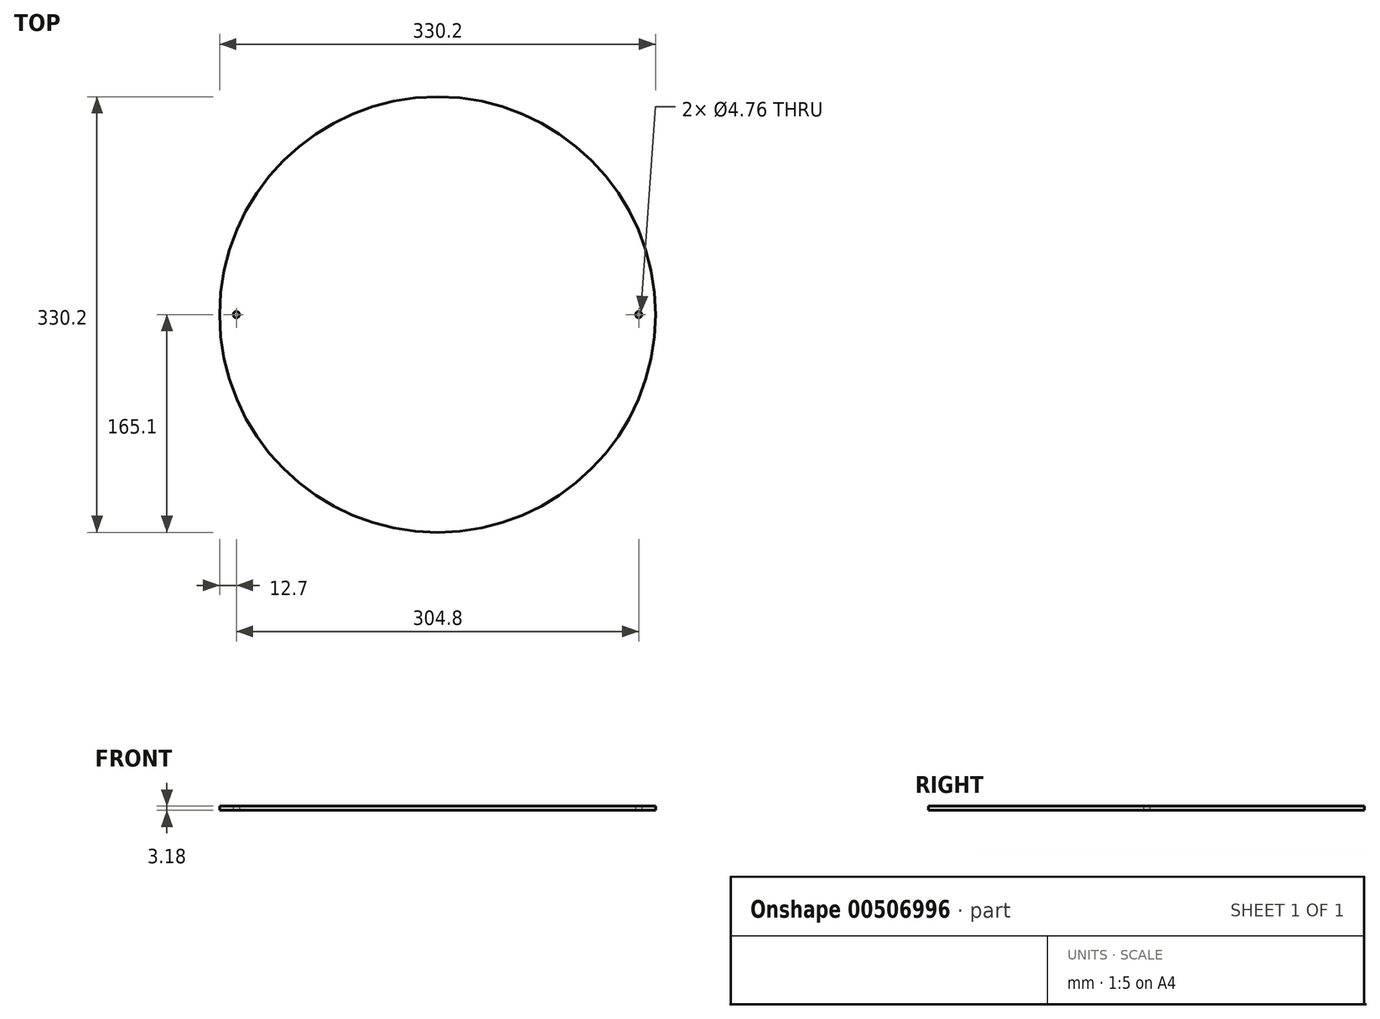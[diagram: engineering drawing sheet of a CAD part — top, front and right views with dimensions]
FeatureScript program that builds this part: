
annotation { "Feature Type Name" : "Feature", "Feature Type Description" : "" }
export const myFeature = defineFeature(function(context is Context, id is Id, definition is map)
    precondition{}
    {
        {
            var Q0;
            Q0=qCreatedBy(makeId("Top.planeOp"),FACE);
            var sketch = newSketch(context, id + "F0", { "sketchPlane" : qUnion([Q0])});
            skCircle(sketch, "E0", {"center": v(0, 0) * mm, "radius": 165.1 * mm});
            skCircle(sketch, "E1", {"center": v(0, 0) * mm, "radius": 139.7 * mm});
            skCircle(sketch, "E2", {"center": v(0, 0) * mm, "radius": 152.4 * mm, "construction": true});
            skLineSegment(sketch, "E3", {"start": v(-165.1, 0) * mm, "end": v(179.95, 0) * mm, "construction": true});
            skCircle(sketch, "E4", {"center": v(-152.4, 0) * mm, "radius": 2.38 * mm});
            skCircle(sketch, "E5.MirrorC", {"center": v(152.4, 0) * mm, "radius": 2.38 * mm});
            skSolve(sketch);
        }
        {
            var Q0;
            Q0 = qSketchRegion(id + "F0", true);
            var Q1;
            Q1=makeQuery(id+"F0.imprint","IMPRINT",FACE,{"disambiguationData":[TD([[makeQuery(id+"F0.imprint","IMPRINT",EDGE,{"derivedFrom":sQuery(id+"F0.wireOp",EDGE,"E1")}),1.0]])]});
            extrude(context, id + "F1", {"entities" : qUnion([Q0, Q1]), "depth" : 3.17 * mm});
        }
    });
